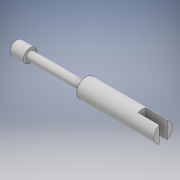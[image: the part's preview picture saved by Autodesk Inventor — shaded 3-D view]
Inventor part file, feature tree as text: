
AUTODESK INVENTOR PART (.ipt)
format: ipt  version: 2017 (Build 210142000, 142)  size: 115,712 bytes
history: native  units: mm
features: extrude x4, sketch x4
ambient origin geometry x8: Origin, YZ Plane, XZ Plane, XY Plane, X Axis, Y Axis, Z Axis, Center Point
bodies: Solid1 (feature_tree)
feature tree (8):
  extrude  "Extrusion1"  Depth=29.0mm TaperAngle=0.0deg
  extrude  "Extrusion2"  Depth=3.0mm
  extrude  "Extrusion3"  Depth=3.0mm
  extrude  "Extrusion4"  Depth=5.0mm
  sketch  "Sketch1"  dims[d0=7.0mm d1=29.0mm d2=0.0mm]
  sketch  "Sketch2"  dims[d3=10.0mm d4=3.0mm]
  sketch  "Sketch3"  dims[d5=8.0mm d6=0.0mm d7=3.0mm]
  sketch  "Sketch4"  dims[d8=26.0mm d9=0.0mm d10=5.0mm d11=5.0mm d12=0.0mm]
